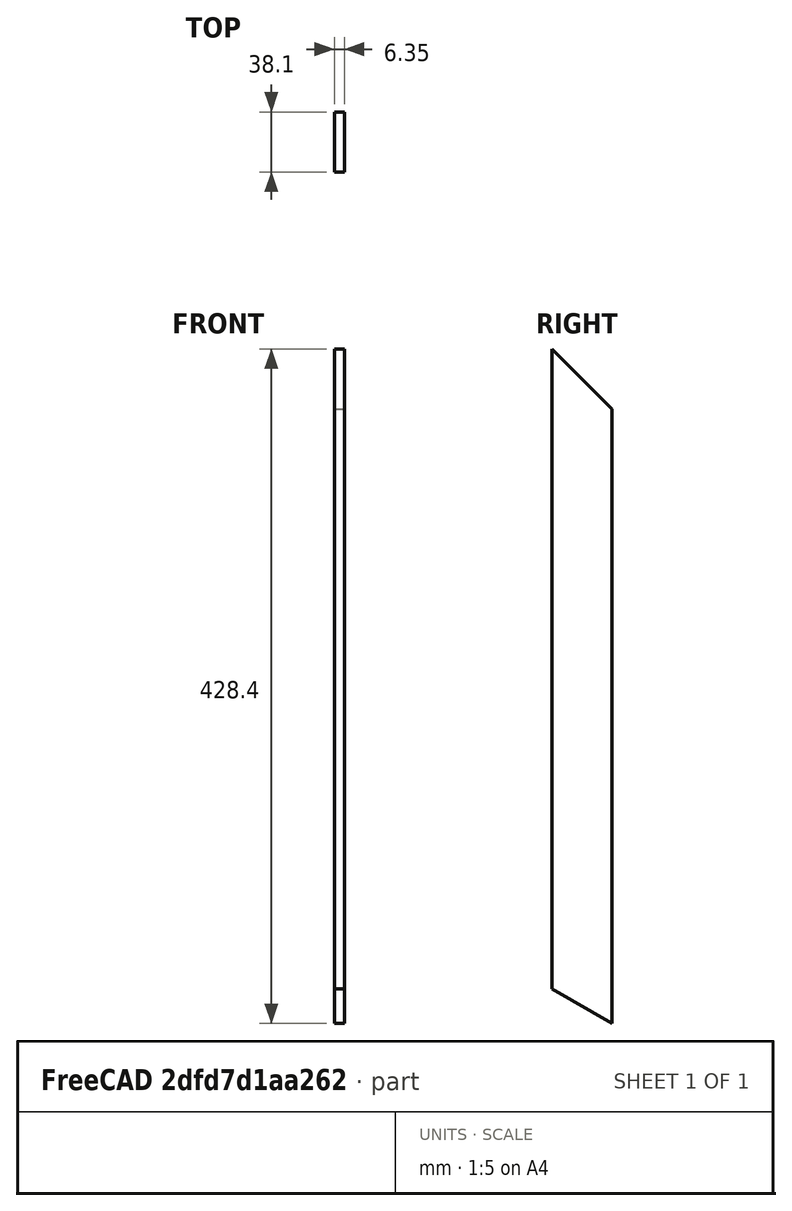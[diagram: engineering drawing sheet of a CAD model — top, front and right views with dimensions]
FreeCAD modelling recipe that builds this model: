
FCSTD DOCUMENT  (FreeCAD 0.17R13387 (Git))
Label: ssqa side bar
License: CreativeCommons Attribution
LicenseURL: http://creativecommons.org/licenses/by/4.0/
objects: Sketcher::SketchObject×1, PartDesign::Pad×1, PartDesign::Body×1
note: 4 computed .brp shape members not serialized (recipe doc carries the construction recipe); baked Part::Feature solids carry a one-line shape summary decoded from their .brp

FEATURE [Sketcher::SketchObject] Sketch
  MapMode = 5
  Placement = pos=(0,0,0) rot=(0.57735,0.57735,0.57735;2.0944rad)
  Support = -> [YZ_Plane]
  sketch-geometry (4):
    g0: LineSegment StartX=0 StartY=0 StartZ=0 EndX=0 EndY=-406.4 EndZ=0
    g1: LineSegment StartX=0 StartY=-406.4 StartZ=0 EndX=38.1 EndY=-428.397 EndZ=0
    g2: LineSegment StartX=38.1 StartY=-428.397 StartZ=0 EndX=38.1 EndY=-38.1 EndZ=0
    g3: LineSegment StartX=38.1 StartY=-38.1 StartZ=0 EndX=0 EndY=0 EndZ=0
  constraints (11):
    c: Coincident(g-1,g0)
    c: Vertical(g0)
    c: Coincident(g0,g1)
    c: Coincident(g1,g2)
    c: Vertical(g2)
    c: Coincident(g2,g3)
    c: Coincident(g3,g0)
    c: DistanceY(g0,g0) = 406.4
    c: Angle(g1,g0) = 2.0944
    c: Angle(g0,g3) = 0.785398
    c: DistanceX(g-1,g2) = 38.1
FEATURE [PartDesign::Pad] Pad
  Length = 6.35
  Length2 = 100.076
  Placement = pos=(0,0,0) rot=(0.57735,0.57735,0.57735;2.0944rad)
  Profile = -> Sketch
  Type = 0
FEATURE [PartDesign::Body] Body
  Group = -> [Sketch,Pad]
  Origin = -> Origin
  Tip = -> Pad
